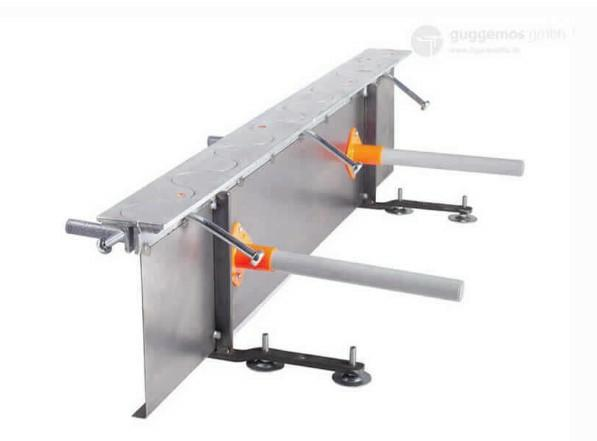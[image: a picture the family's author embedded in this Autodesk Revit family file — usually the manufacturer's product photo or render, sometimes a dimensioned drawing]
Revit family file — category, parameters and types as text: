
# Revit family: Herkules ERL_Fugenprofile mit Sinuswelle Dehnfugenprofil Tagesfeldabschalung
name_source: partatom
category: Generic Models
units: mm (PartAtom-declared; Revit-internal decimal feet)

## family parameters
Always vertical = No
Can host rebar = No
Cut with Voids When Loaded = No
Part Type = Normal
Room Calculation Point = No
Round Connector Dimension = Use Diameter
Shared = No
Work Plane-Based = Yes

## types (1)
- Herkules_ERL_L2500_H500
    Adresse = Iglauer Str. 6 86316 Friedberg
    Default Elevation = 0 mm  [stored 0 ft]
    Delivery time = 2 weeks
    Description = Schwerlastfugenprofil für industriell genutzte Betonbodenplatten
    Keynote = Herkules
    Manufacturer = Guggemos GmbH
    Model = Schwerlastfugenprofil zur Bauteilentkopplung
    Telephone = +49 (0)8 21 / 455 969 0
    Type Comments = HerkulesERL_L2500
    Type Image = Herkules ERL_foto.jpg (2)
    URL = https://www.fugenprofile.de
    Video = https://www.youtube.com

note: [stored X ft] marks values corroborated as IEEE doubles in the binary element streams (Revit-internal decimal feet)

## geometry (parser evidence)
native form markers: Sweep x15
no freeform markers — native parametric forms only
